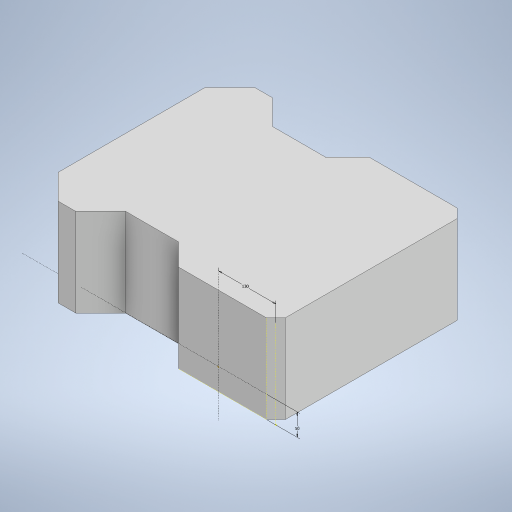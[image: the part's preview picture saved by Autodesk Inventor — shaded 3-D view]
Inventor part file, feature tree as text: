
AUTODESK INVENTOR PART (.ipt)
format: ipt  version: 2024 (Build 280153000, 153)  size: 222,208 bytes
history: native  units: mm
features: other x2, sketch x2, extrude x1
ambient origin geometry x8: Origin, YZ Plane, XZ Plane, XY Plane, X Axis, Y Axis, Z Axis, Center Point
bodies: Solid1 (feature_tree)
feature tree (5):
  other  "Frame"
  extrude  "Extrusion1"  Depth=390.0mm
  sketch  "Sketch2"  dims[d2=45.0deg d3=70.0mm d4=135.0deg d5=200.0mm d6=120.0mm d7=80.0mm d8=135.0deg d9=226.066017mm d10=21.213203mm d11=40.0mm d12=80.0mm d15=543.847763mm d16=200.0mm d17=0.0mm d18=50.0mm d19=130.0mm]
  other  "Work Point1"
  sketch  "Sketch1"  dims[d0=390.0mm d1=30.0mm]
